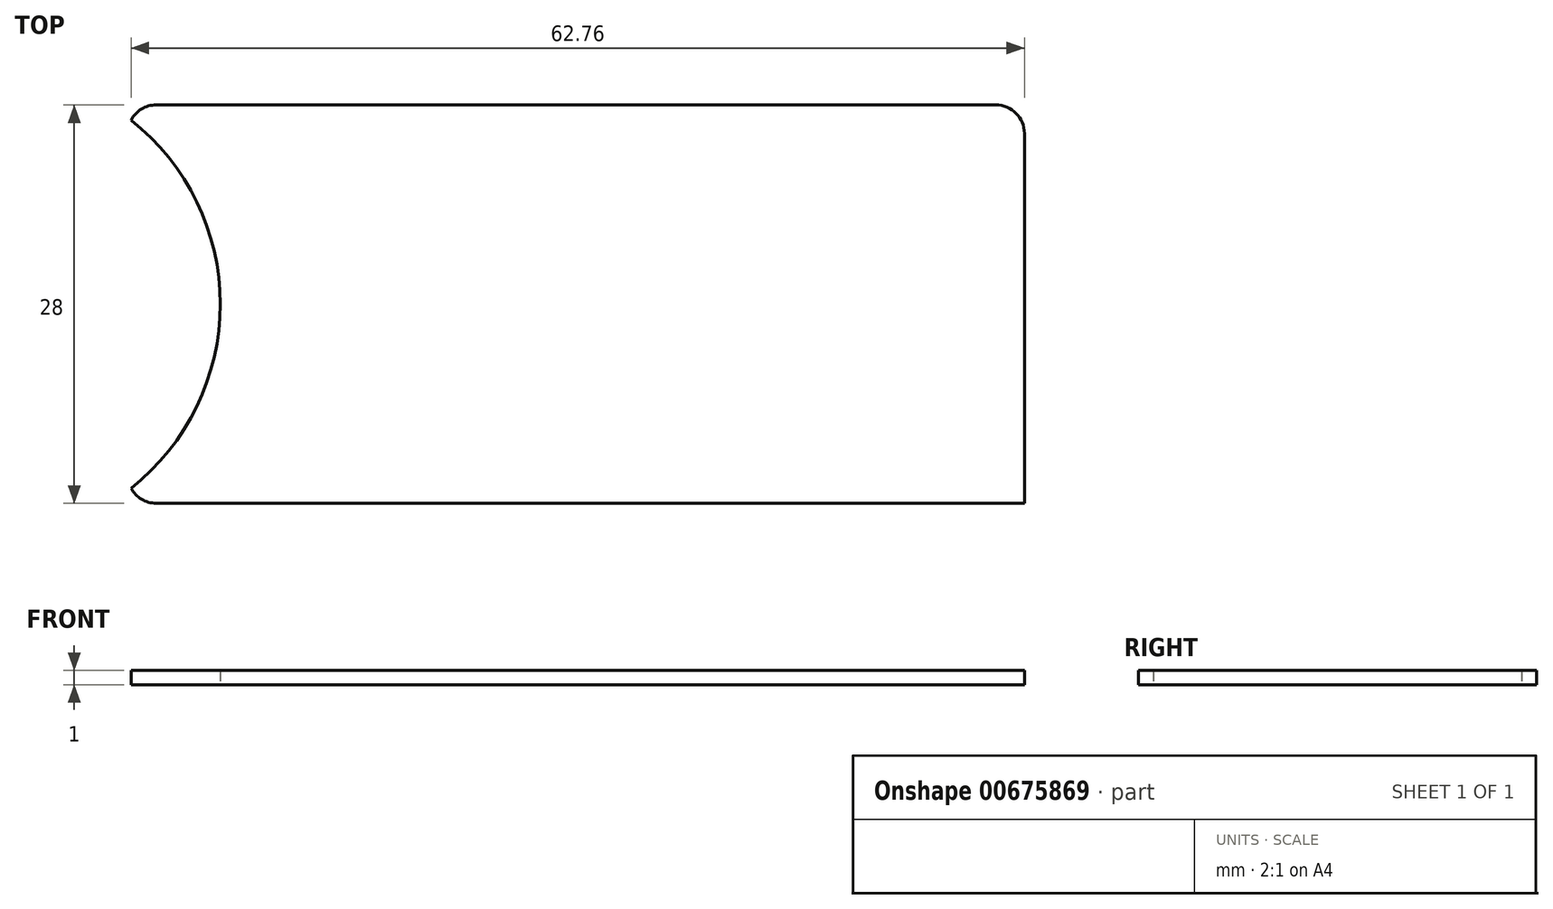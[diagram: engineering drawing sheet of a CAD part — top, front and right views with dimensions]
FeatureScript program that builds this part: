
annotation { "Feature Type Name" : "Feature", "Feature Type Description" : "" }
export const myFeature = defineFeature(function(context is Context, id is Id, definition is map)
    precondition{}
    {
        {
            var Q0;
            Q0=qCreatedBy(makeId("Top.planeOp"),FACE);
            var sketch = newSketch(context, id + "F0", { "sketchPlane" : qUnion([Q0])});
            skLineSegment(sketch, "E0.bottom", {"start": v(2, 0) * mm, "end": v(63, 0) * mm});
            skLineSegment(sketch, "E0.top", {"start": v(2, 28) * mm, "end": v(61, 28) * mm});
            skLineSegment(sketch, "E0.left", {"start": v(0, 2) * mm, "end": v(0, 26) * mm});
            skLineSegment(sketch, "E0.right", {"start": v(63, 0) * mm, "end": v(63, 26) * mm});
            skPoint(sketch, "E1.visualSharp", {"position": v(0, 28) * mm});
            skArc(sketch, "E1.filletArc", {"start": v(2, 28) * mm, "mid": v(0.59, 27.41) * mm, "end": v(0, 26) * mm});
            skPoint(sketch, "E2.visualSharp", {"position": v(0, 0) * mm});
            skArc(sketch, "E2.filletArc", {"start": v(0, 2) * mm, "mid": v(0.59, 0.59) * mm, "end": v(2, 0) * mm});
            skPoint(sketch, "E3.visualSharp", {"position": v(63, 0) * mm});
            skLineSegment(sketch, "E3.filletArc", {"start": v(63, 0) * mm, "end": v(63, 0) * mm});
            skPoint(sketch, "E4.visualSharp", {"position": v(63, 28) * mm});
            skArc(sketch, "E4.filletArc", {"start": v(63, 26) * mm, "mid": v(62.41, 27.41) * mm, "end": v(61, 28) * mm});
            skLineSegment(sketch, "E5", {"start": v(0, 14) * mm, "end": v(-10, 14) * mm});
            skCircle(sketch, "E6", {"center": v(-10, 14) * mm, "radius": 16.5 * mm});
            skSolve(sketch);
        }
        {
            var Q0;
            Q0=makeQuery(id+"F0.imprint","IMPRINT",FACE,{"disambiguationData":[TD([[makeQuery(id+"F0.imprint","IMPRINT",EDGE,{"derivedFrom":sQuery(id+"F0.wireOp",EDGE,"E0.bottom")}),1.0]])]});
            extrude(context, id + "F1", {"entities" : qUnion([Q0]), "depth" : 1 * mm, "offsetDistance" : 25.4 * mm});
        }
    });
